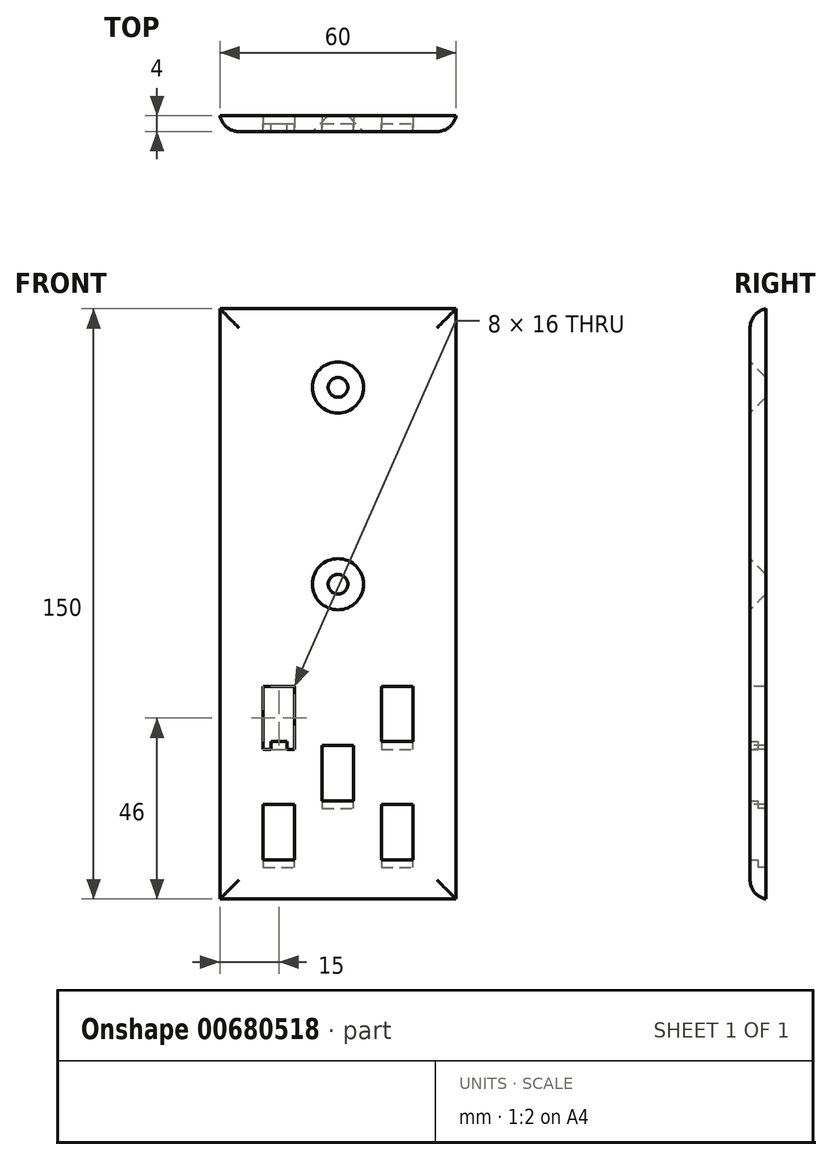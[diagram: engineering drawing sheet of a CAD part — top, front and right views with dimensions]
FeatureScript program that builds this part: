
annotation { "Feature Type Name" : "Feature", "Feature Type Description" : "" }
export const myFeature = defineFeature(function(context is Context, id is Id, definition is map)
    precondition{}
    {
        {
            var Q0;
            Q0=qCreatedBy(makeId("Front.planeOp"),FACE);
            var sketch = newSketch(context, id + "F0", { "sketchPlane" : qUnion([Q0])});
            skLineSegment(sketch, "E0", {"start": v(0, 0) * mm, "end": v(-30, 0) * mm});
            skLineSegment(sketch, "E1", {"start": v(-30, 0) * mm, "end": v(30, 0) * mm});
            skLineSegment(sketch, "E2", {"start": v(30, 0) * mm, "end": v(30, 80) * mm});
            skLineSegment(sketch, "E3", {"start": v(30, 80) * mm, "end": v(-30, 80) * mm});
            skLineSegment(sketch, "E4", {"start": v(-30, 80) * mm, "end": v(-30, 0) * mm});
            skLineSegment(sketch, "E5", {"start": v(-30, 0) * mm, "end": v(-30, 50) * mm, "construction": true});
            skLineSegment(sketch, "E6", {"start": v(-30, 50) * mm, "end": v(30, 50) * mm, "construction": true});
            skLineSegment(sketch, "E7", {"start": v(30, 50) * mm, "end": v(0, 50) * mm, "construction": true});
            skLineSegment(sketch, "E8", {"start": v(0, 50) * mm, "end": v(0, 20) * mm, "construction": true});
            skLineSegment(sketch, "E9", {"start": v(0, 20) * mm, "end": v(30, 20) * mm, "construction": true});
            skLineSegment(sketch, "E10", {"start": v(30, 20) * mm, "end": v(-30, 20) * mm, "construction": true});
            skPoint(sketch, "E10.endSnap0", {"position": v(15, 20) * mm});
            skLineSegment(sketch, "E11.bottom", {"start": v(15, 50) * mm, "end": v(-15, 50) * mm, "construction": true});
            skLineSegment(sketch, "E11.top", {"start": v(15, 20) * mm, "end": v(-15, 20) * mm, "construction": true});
            skLineSegment(sketch, "E11.left", {"start": v(15, 50) * mm, "end": v(15, 20) * mm, "construction": true});
            skLineSegment(sketch, "E11.right", {"start": v(-15, 50) * mm, "end": v(-15, 20) * mm, "construction": true});
            skPoint(sketch, "E11.middle", {"position": v(0, 35) * mm});
            skLineSegment(sketch, "E12", {"start": v(-15, 50) * mm, "end": v(15, 20) * mm, "construction": true});
            skLineSegment(sketch, "E13", {"start": v(15, 50) * mm, "end": v(-15, 20) * mm, "construction": true});
            skLineSegment(sketch, "E14.bottom", {"start": v(-11, 46) * mm, "end": v(-19, 46) * mm});
            skLineSegment(sketch, "E14.top", {"start": v(-11, 54) * mm, "end": v(-19, 54) * mm});
            skLineSegment(sketch, "E14.left", {"start": v(-11, 46) * mm, "end": v(-11, 54) * mm});
            skLineSegment(sketch, "E14.right", {"start": v(-19, 46) * mm, "end": v(-19, 54) * mm});
            skPoint(sketch, "E14.middle", {"position": v(-15, 50) * mm});
            skLineSegment(sketch, "E15.bottom", {"start": v(19, 46) * mm, "end": v(11, 46) * mm});
            skLineSegment(sketch, "E15.top", {"start": v(19, 54) * mm, "end": v(11, 54) * mm});
            skLineSegment(sketch, "E15.left", {"start": v(19, 46) * mm, "end": v(19, 54) * mm});
            skLineSegment(sketch, "E15.right", {"start": v(11, 46) * mm, "end": v(11, 54) * mm});
            skPoint(sketch, "E15.middle", {"position": v(15, 50) * mm});
            skLineSegment(sketch, "E16.bottom", {"start": v(4, 31) * mm, "end": v(-4, 31) * mm});
            skLineSegment(sketch, "E16.top", {"start": v(4, 39) * mm, "end": v(-4, 39) * mm});
            skLineSegment(sketch, "E16.left", {"start": v(4, 31) * mm, "end": v(4, 39) * mm});
            skLineSegment(sketch, "E16.right", {"start": v(-4, 31) * mm, "end": v(-4, 39) * mm});
            skLineSegment(sketch, "E17.bottom", {"start": v(-11, 16) * mm, "end": v(-19, 16) * mm});
            skLineSegment(sketch, "E17.top", {"start": v(-11, 24) * mm, "end": v(-19, 24) * mm});
            skLineSegment(sketch, "E17.left", {"start": v(-11, 16) * mm, "end": v(-11, 24) * mm});
            skLineSegment(sketch, "E17.right", {"start": v(-19, 16) * mm, "end": v(-19, 24) * mm});
            skPoint(sketch, "E17.middle", {"position": v(-15, 20) * mm});
            skLineSegment(sketch, "E18.bottom", {"start": v(19, 16) * mm, "end": v(11, 16) * mm});
            skLineSegment(sketch, "E18.top", {"start": v(19, 24) * mm, "end": v(11, 24) * mm});
            skLineSegment(sketch, "E18.left", {"start": v(19, 16) * mm, "end": v(19, 24) * mm});
            skLineSegment(sketch, "E18.right", {"start": v(11, 16) * mm, "end": v(11, 24) * mm});
            skLineSegment(sketch, "E19.bottom", {"start": v(-19, 46) * mm, "end": v(-11, 46) * mm});
            skLineSegment(sketch, "E19.left", {"start": v(-19, 46) * mm, "end": v(-19, 48) * mm});
            skLineSegment(sketch, "E19.right", {"start": v(-11, 46) * mm, "end": v(-11, 48) * mm});
            skLineSegment(sketch, "E20.top", {"start": v(-19, 38) * mm, "end": v(-11, 38) * mm});
            skLineSegment(sketch, "E20.left", {"start": v(-19, 46) * mm, "end": v(-19, 38) * mm});
            skLineSegment(sketch, "E20.right", {"start": v(-11, 46) * mm, "end": v(-11, 38) * mm});
            skLineSegment(sketch, "E21.bottom", {"start": v(11, 46) * mm, "end": v(19, 46) * mm});
            skLineSegment(sketch, "E21.top", {"start": v(11, 38) * mm, "end": v(19, 38) * mm});
            skLineSegment(sketch, "E21.left", {"start": v(11, 46) * mm, "end": v(11, 38) * mm});
            skLineSegment(sketch, "E21.right", {"start": v(19, 46) * mm, "end": v(19, 38) * mm});
            skLineSegment(sketch, "E22.bottom", {"start": v(-4, 31) * mm, "end": v(4, 31) * mm});
            skLineSegment(sketch, "E22.top", {"start": v(-4, 23) * mm, "end": v(4, 23) * mm});
            skLineSegment(sketch, "E22.left", {"start": v(-4, 31) * mm, "end": v(-4, 23) * mm});
            skLineSegment(sketch, "E22.right", {"start": v(4, 31) * mm, "end": v(4, 23) * mm});
            skLineSegment(sketch, "E23.bottom", {"start": v(-19, 16) * mm, "end": v(-11, 16) * mm});
            skLineSegment(sketch, "E23.top", {"start": v(-19, 8) * mm, "end": v(-11, 8) * mm});
            skLineSegment(sketch, "E23.left", {"start": v(-19, 16) * mm, "end": v(-19, 8) * mm});
            skLineSegment(sketch, "E23.right", {"start": v(-11, 16) * mm, "end": v(-11, 8) * mm});
            skLineSegment(sketch, "E24.bottom", {"start": v(11, 16) * mm, "end": v(19, 16) * mm});
            skLineSegment(sketch, "E24.top", {"start": v(11, 8) * mm, "end": v(19, 8) * mm});
            skLineSegment(sketch, "E24.left", {"start": v(11, 16) * mm, "end": v(11, 8) * mm});
            skLineSegment(sketch, "E24.right", {"start": v(19, 16) * mm, "end": v(19, 8) * mm});
            skLineSegment(sketch, "E25.bottom", {"start": v(-4, 31) * mm, "end": v(-2, 31) * mm});
            skLineSegment(sketch, "E25.top", {"start": v(-4, 23) * mm, "end": v(-2, 23) * mm});
            skLineSegment(sketch, "E25.right", {"start": v(-2, 31) * mm, "end": v(-2, 23) * mm});
            skLineSegment(sketch, "E26.bottom", {"start": v(-2, 31) * mm, "end": v(2, 31) * mm});
            skLineSegment(sketch, "E26.top", {"start": v(-2, 23) * mm, "end": v(2, 23) * mm});
            skLineSegment(sketch, "E26.right", {"start": v(2, 31) * mm, "end": v(2, 23) * mm});
            skLineSegment(sketch, "E27.bottom", {"start": v(-19, 46) * mm, "end": v(-17, 46) * mm});
            skLineSegment(sketch, "E27.top", {"start": v(-19, 38) * mm, "end": v(-17, 38) * mm});
            skLineSegment(sketch, "E27.right", {"start": v(-17, 46) * mm, "end": v(-17, 38) * mm});
            skLineSegment(sketch, "E28.bottom", {"start": v(-11, 46) * mm, "end": v(-13, 46) * mm});
            skLineSegment(sketch, "E28.top", {"start": v(-11, 38) * mm, "end": v(-13, 38) * mm});
            skLineSegment(sketch, "E28.right", {"start": v(-13, 46) * mm, "end": v(-13, 38) * mm});
            skLineSegment(sketch, "E29.bottom", {"start": v(11, 46) * mm, "end": v(13, 46) * mm});
            skLineSegment(sketch, "E29.top", {"start": v(11, 38) * mm, "end": v(13, 38) * mm});
            skLineSegment(sketch, "E29.right", {"start": v(13, 46) * mm, "end": v(13, 38) * mm});
            skLineSegment(sketch, "E30.bottom", {"start": v(19, 46) * mm, "end": v(17, 46) * mm});
            skLineSegment(sketch, "E30.top", {"start": v(19, 38) * mm, "end": v(17, 38) * mm});
            skLineSegment(sketch, "E30.right", {"start": v(17, 46) * mm, "end": v(17, 38) * mm});
            skLineSegment(sketch, "E31.bottom", {"start": v(19, 16) * mm, "end": v(17, 16) * mm});
            skLineSegment(sketch, "E31.top", {"start": v(19, 8) * mm, "end": v(17, 8) * mm});
            skLineSegment(sketch, "E32.bottom", {"start": v(-11, 16) * mm, "end": v(-13, 16) * mm});
            skLineSegment(sketch, "E32.top", {"start": v(-11, 8) * mm, "end": v(-13, 8) * mm});
            skLineSegment(sketch, "E32.right", {"start": v(-13, 16) * mm, "end": v(-13, 8) * mm});
            skLineSegment(sketch, "E33.right", {"start": v(17, 16) * mm, "end": v(17, 8) * mm});
            skLineSegment(sketch, "E34.bottom", {"start": v(11, 16) * mm, "end": v(13, 16) * mm});
            skLineSegment(sketch, "E34.top", {"start": v(11, 8) * mm, "end": v(13, 8) * mm});
            skLineSegment(sketch, "E34.right", {"start": v(13, 16) * mm, "end": v(13, 8) * mm});
            skLineSegment(sketch, "E35.bottom", {"start": v(-19, 16) * mm, "end": v(-17, 16) * mm});
            skLineSegment(sketch, "E35.top", {"start": v(-19, 8) * mm, "end": v(-17, 8) * mm});
            skLineSegment(sketch, "E35.right", {"start": v(-17, 16) * mm, "end": v(-17, 8) * mm});
            skLineSegment(sketch, "E36.top", {"start": v(-19, 40) * mm, "end": v(-11, 40) * mm});
            skLineSegment(sketch, "E36.left", {"start": v(-19, 38) * mm, "end": v(-19, 40) * mm});
            skLineSegment(sketch, "E36.right", {"start": v(-11, 38) * mm, "end": v(-11, 40) * mm});
            skLineSegment(sketch, "E37", {"start": v(11, 40) * mm, "end": v(19, 40) * mm});
            skLineSegment(sketch, "E38", {"start": v(4, 25) * mm, "end": v(-4, 25) * mm});
            skLineSegment(sketch, "E39", {"start": v(-11, 10) * mm, "end": v(-19, 10) * mm});
            skLineSegment(sketch, "E40", {"start": v(11, 10) * mm, "end": v(19, 10) * mm});
            skLineSegment(sketch, "E41.top", {"start": v(-30, 150) * mm, "end": v(30, 150) * mm});
            skLineSegment(sketch, "E41.left", {"start": v(-30, 0) * mm, "end": v(-30, 150) * mm});
            skLineSegment(sketch, "E41.right", {"start": v(30, 0) * mm, "end": v(30, 150) * mm});
            skLineSegment(sketch, "E42", {"start": v(0, 150) * mm, "end": v(0, 80) * mm, "construction": true});
            skLineSegment(sketch, "E43", {"start": v(0, 80) * mm, "end": v(0, 50) * mm, "construction": true});
            skLineSegment(sketch, "E44", {"start": v(0, 150) * mm, "end": v(0, 130) * mm, "construction": true});
            skLineSegment(sketch, "E45", {"start": v(0, 130) * mm, "end": v(0, 80) * mm, "construction": true});
            skCircle(sketch, "E46", {"center": v(0, 130) * mm, "radius": 1.5 * mm});
            skCircle(sketch, "E47", {"center": v(0, 80) * mm, "radius": 1.5 * mm});
            skSolve(sketch);
        }
        {
            var Q0;
            {var subQ3=sQuery(id+"F0.wireOp",EDGE,"E41.top");Q0=makeQuery(id+"F0.imprint","IMPRINT",FACE,{"disambiguationData":[TD([[makeQuery(id+"F0.imprint","IMPRINT",EDGE,{"derivedFrom":subQ3}),-1.0]])]});}
            var Q1;
            Q1=makeQuery(id+"F0.imprint","IMPRINT",FACE,{"disambiguationData":[TD([[makeQuery(id+"F0.imprint","IMPRINT",EDGE,{"derivedFrom":sQuery(id+"F0.wireOp",EDGE,"E14.top")}),-1.0]])]});
            extrude(context, id + "F1", {"entities" : qUnion([Q0, Q1]), "oppositeDirection" : true, "depth" : 2 * mm, "offsetDistance" : 25 * mm});
        }
        {
            var Q0;
            {var subQ0=sQuery(id+"F0.wireOp",EDGE,"E27.bottom");Q0=makeQuery(id+"F0.imprint","IMPRINT",FACE,{"disambiguationData":[TD([[makeQuery(id+"F0.imprint","IMPRINT",EDGE,{"derivedFrom":subQ0}),-1.0]])]});}
            var Q1;
            {var subQ5=sQuery(id+"F0.wireOp",EDGE,"E36.left");Q1=makeQuery(id+"F0.imprint","IMPRINT",FACE,{"disambiguationData":[TD([[makeQuery(id+"F0.imprint","IMPRINT",EDGE,{"derivedFrom":subQ5}),-1.0]])]});}
            var Q2;
            {var subQ0=sQuery(id+"F0.wireOp",EDGE,"E20.top");var subQ1=sQuery(id+"F0.wireOp",EDGE,"E27.right");var subQ2=makeQuery(id+"F0.imprint","INTERSECT",VERTEX,{"derivedFrom":[subQ1,subQ0]});Q2=makeQuery(id+"F0.imprint","IMPRINT",FACE,{"disambiguationData":[TD([[makeQuery(id+"F0.imprint","IMPRINT",EDGE,{"disambiguationData":[TD([[subQ2,1.0]])],"derivedFrom":subQ1}),1.0]])]});}
            var Q3;
            {var subQ5=sQuery(id+"F0.wireOp",EDGE,"E36.right");Q3=makeQuery(id+"F0.imprint","IMPRINT",FACE,{"disambiguationData":[TD([[makeQuery(id+"F0.imprint","IMPRINT",EDGE,{"derivedFrom":subQ5}),1.0]])]});}
            var Q4;
            {var subQ0=sQuery(id+"F0.wireOp",EDGE,"E28.bottom");Q4=makeQuery(id+"F0.imprint","IMPRINT",FACE,{"disambiguationData":[TD([[makeQuery(id+"F0.imprint","IMPRINT",EDGE,{"derivedFrom":subQ0}),1.0]])]});}
            var Q5;
            {var subQ0=sQuery(id+"F0.wireOp",EDGE,"E29.bottom");Q5=makeQuery(id+"F0.imprint","IMPRINT",FACE,{"disambiguationData":[TD([[makeQuery(id+"F0.imprint","IMPRINT",EDGE,{"derivedFrom":subQ0}),-1.0]])]});}
            var Q6;
            {var subQ0=sQuery(id+"F0.wireOp",EDGE,"E29.top");Q6=makeQuery(id+"F0.imprint","IMPRINT",FACE,{"disambiguationData":[TD([[makeQuery(id+"F0.imprint","IMPRINT",EDGE,{"derivedFrom":subQ0}),1.0]])]});}
            var Q7;
            {var subQ0=sQuery(id+"F0.wireOp",EDGE,"E21.top");Q7=makeQuery(id+"F0.imprint","IMPRINT",FACE,{"disambiguationData":[TD([[makeQuery(id+"F0.imprint","IMPRINT",EDGE,{"derivedFrom":subQ0}),1.0]])]});}
            var Q8;
            {var subQ0=sQuery(id+"F0.wireOp",EDGE,"E30.top");Q8=makeQuery(id+"F0.imprint","IMPRINT",FACE,{"disambiguationData":[TD([[makeQuery(id+"F0.imprint","IMPRINT",EDGE,{"derivedFrom":subQ0}),-1.0]])]});}
            var Q9;
            {var subQ0=sQuery(id+"F0.wireOp",EDGE,"E30.bottom");Q9=makeQuery(id+"F0.imprint","IMPRINT",FACE,{"disambiguationData":[TD([[makeQuery(id+"F0.imprint","IMPRINT",EDGE,{"derivedFrom":subQ0}),1.0]])]});}
            var Q10;
            {var subQ0=sQuery(id+"F0.wireOp",EDGE,"E22.bottom");Q10=makeQuery(id+"F0.imprint","IMPRINT",FACE,{"disambiguationData":[TD([[makeQuery(id+"F0.imprint","IMPRINT",EDGE,{"derivedFrom":subQ0}),-1.0]])]});}
            var Q11;
            {var subQ0=sQuery(id+"F0.wireOp",EDGE,"E22.top");Q11=makeQuery(id+"F0.imprint","IMPRINT",FACE,{"disambiguationData":[TD([[makeQuery(id+"F0.imprint","IMPRINT",EDGE,{"derivedFrom":subQ0}),1.0]])]});}
            var Q12;
            {var subQ0=sQuery(id+"F0.wireOp",EDGE,"E26.top");Q12=makeQuery(id+"F0.imprint","IMPRINT",FACE,{"disambiguationData":[TD([[makeQuery(id+"F0.imprint","IMPRINT",EDGE,{"derivedFrom":subQ0}),1.0]])]});}
            var Q13;
            {var subQ0=sQuery(id+"F0.wireOp",EDGE,"E25.top");Q13=makeQuery(id+"F0.imprint","IMPRINT",FACE,{"disambiguationData":[TD([[makeQuery(id+"F0.imprint","IMPRINT",EDGE,{"derivedFrom":subQ0}),1.0]])]});}
            var Q14;
            {var subQ0=sQuery(id+"F0.wireOp",EDGE,"E25.bottom");Q14=makeQuery(id+"F0.imprint","IMPRINT",FACE,{"disambiguationData":[TD([[makeQuery(id+"F0.imprint","IMPRINT",EDGE,{"derivedFrom":subQ0}),-1.0]])]});}
            var Q15;
            {var subQ0=sQuery(id+"F0.wireOp",EDGE,"E35.bottom");Q15=makeQuery(id+"F0.imprint","IMPRINT",FACE,{"disambiguationData":[TD([[makeQuery(id+"F0.imprint","IMPRINT",EDGE,{"derivedFrom":subQ0}),-1.0]])]});}
            var Q16;
            {var subQ0=sQuery(id+"F0.wireOp",EDGE,"E35.top");Q16=makeQuery(id+"F0.imprint","IMPRINT",FACE,{"disambiguationData":[TD([[makeQuery(id+"F0.imprint","IMPRINT",EDGE,{"derivedFrom":subQ0}),1.0]])]});}
            var Q17;
            {var subQ0=sQuery(id+"F0.wireOp",EDGE,"E23.top");Q17=makeQuery(id+"F0.imprint","IMPRINT",FACE,{"disambiguationData":[TD([[makeQuery(id+"F0.imprint","IMPRINT",EDGE,{"derivedFrom":subQ0}),1.0]])]});}
            var Q18;
            {var subQ0=sQuery(id+"F0.wireOp",EDGE,"E32.top");Q18=makeQuery(id+"F0.imprint","IMPRINT",FACE,{"disambiguationData":[TD([[makeQuery(id+"F0.imprint","IMPRINT",EDGE,{"derivedFrom":subQ0}),-1.0]])]});}
            var Q19;
            {var subQ0=sQuery(id+"F0.wireOp",EDGE,"E32.bottom");Q19=makeQuery(id+"F0.imprint","IMPRINT",FACE,{"disambiguationData":[TD([[makeQuery(id+"F0.imprint","IMPRINT",EDGE,{"derivedFrom":subQ0}),1.0]])]});}
            var Q20;
            {var subQ0=sQuery(id+"F0.wireOp",EDGE,"E34.bottom");Q20=makeQuery(id+"F0.imprint","IMPRINT",FACE,{"disambiguationData":[TD([[makeQuery(id+"F0.imprint","IMPRINT",EDGE,{"derivedFrom":subQ0}),-1.0]])]});}
            var Q21;
            {var subQ0=sQuery(id+"F0.wireOp",EDGE,"E34.top");Q21=makeQuery(id+"F0.imprint","IMPRINT",FACE,{"disambiguationData":[TD([[makeQuery(id+"F0.imprint","IMPRINT",EDGE,{"derivedFrom":subQ0}),1.0]])]});}
            var Q22;
            {var subQ0=sQuery(id+"F0.wireOp",EDGE,"E31.bottom");Q22=makeQuery(id+"F0.imprint","IMPRINT",FACE,{"disambiguationData":[TD([[makeQuery(id+"F0.imprint","IMPRINT",EDGE,{"derivedFrom":subQ0}),1.0]])]});}
            var Q23;
            {var subQ0=sQuery(id+"F0.wireOp",EDGE,"E24.top");Q23=makeQuery(id+"F0.imprint","IMPRINT",FACE,{"disambiguationData":[TD([[makeQuery(id+"F0.imprint","IMPRINT",EDGE,{"derivedFrom":subQ0}),1.0]])]});}
            var Q24;
            {var subQ0=sQuery(id+"F0.wireOp",EDGE,"E31.top");Q24=makeQuery(id+"F0.imprint","IMPRINT",FACE,{"disambiguationData":[TD([[makeQuery(id+"F0.imprint","IMPRINT",EDGE,{"derivedFrom":subQ0}),-1.0]])]});}
            var Q25;
            Q25=makeQuery(id+"F0.imprint","IMPRINT",FACE,{"disambiguationData":[TD([[makeQuery(id+"F0.imprint","IMPRINT",EDGE,{"derivedFrom":sQuery(id+"F0.wireOp",EDGE,"E14.top")}),-1.0]])]});
            var Q26;
            {var subQ3=sQuery(id+"F0.wireOp",EDGE,"E41.top");Q26=makeQuery(id+"F0.imprint","IMPRINT",FACE,{"disambiguationData":[TD([[makeQuery(id+"F0.imprint","IMPRINT",EDGE,{"derivedFrom":subQ3}),-1.0]])]});}
            extrude(context, id + "F2", {"entities" : qUnion([Q0, Q1, Q2, Q3, Q4, Q5, Q6, Q7, Q8, Q9, Q10, Q11, Q12, Q13, Q14, Q15, Q16, Q17, Q18, Q19, Q20, Q21, Q22, Q23, Q24, Q25, Q26]), "operationType" : NewBodyOperationType.ADD, "depth" : 2 * mm, "offsetDistance" : 25 * mm});
        }
        {
            var Q0;
            Q0=makeQuery(id+"F2.opExtrude","CAP_EDGE",EDGE,{"disambiguationData":[OSD([sQuery(id+"F0.wireOp",EDGE,"E46")])],"isStart":false});
            var Q1;
            Q1=makeQuery(id+"F2.opExtrude","CAP_EDGE",EDGE,{"disambiguationData":[OSD([sQuery(id+"F0.wireOp",EDGE,"E47")])],"isStart":false});
            chamfer(context, id + "F3", {"entities" : qUnion([Q0, Q1]), "width" : 5 * mm, "tangentPropagation" : true});
        }
        {
            var Q0;
            Q0=makeQuery(id+"F2.opExtrude","CAP_EDGE",EDGE,{"disambiguationData":[OSD([sQuery(id+"F0.wireOp",EDGE,"E1")])],"isStart":false});
            var Q1;
            Q1=makeQuery(id+"F2.opExtrude","CAP_EDGE",EDGE,{"disambiguationData":[OSD([sQuery(id+"F0.wireOp",EDGE,"E41.left")])],"isStart":false});
            var Q2;
            Q2=makeQuery(id+"F2.opExtrude","CAP_EDGE",EDGE,{"disambiguationData":[OSD([sQuery(id+"F0.wireOp",EDGE,"E41.right")])],"isStart":false});
            var Q3;
            Q3=makeQuery(id+"F2.opExtrude","CAP_EDGE",EDGE,{"disambiguationData":[OSD([sQuery(id+"F0.wireOp",EDGE,"E41.top")])],"isStart":false});
            fillet(context, id + "F4", {"entities" : qUnion([Q0, Q1, Q2, Q3]), "radius" : 5 * mm, "tangentPropagation" : true, "allowEdgeOverflow" : false});
        }
    });
